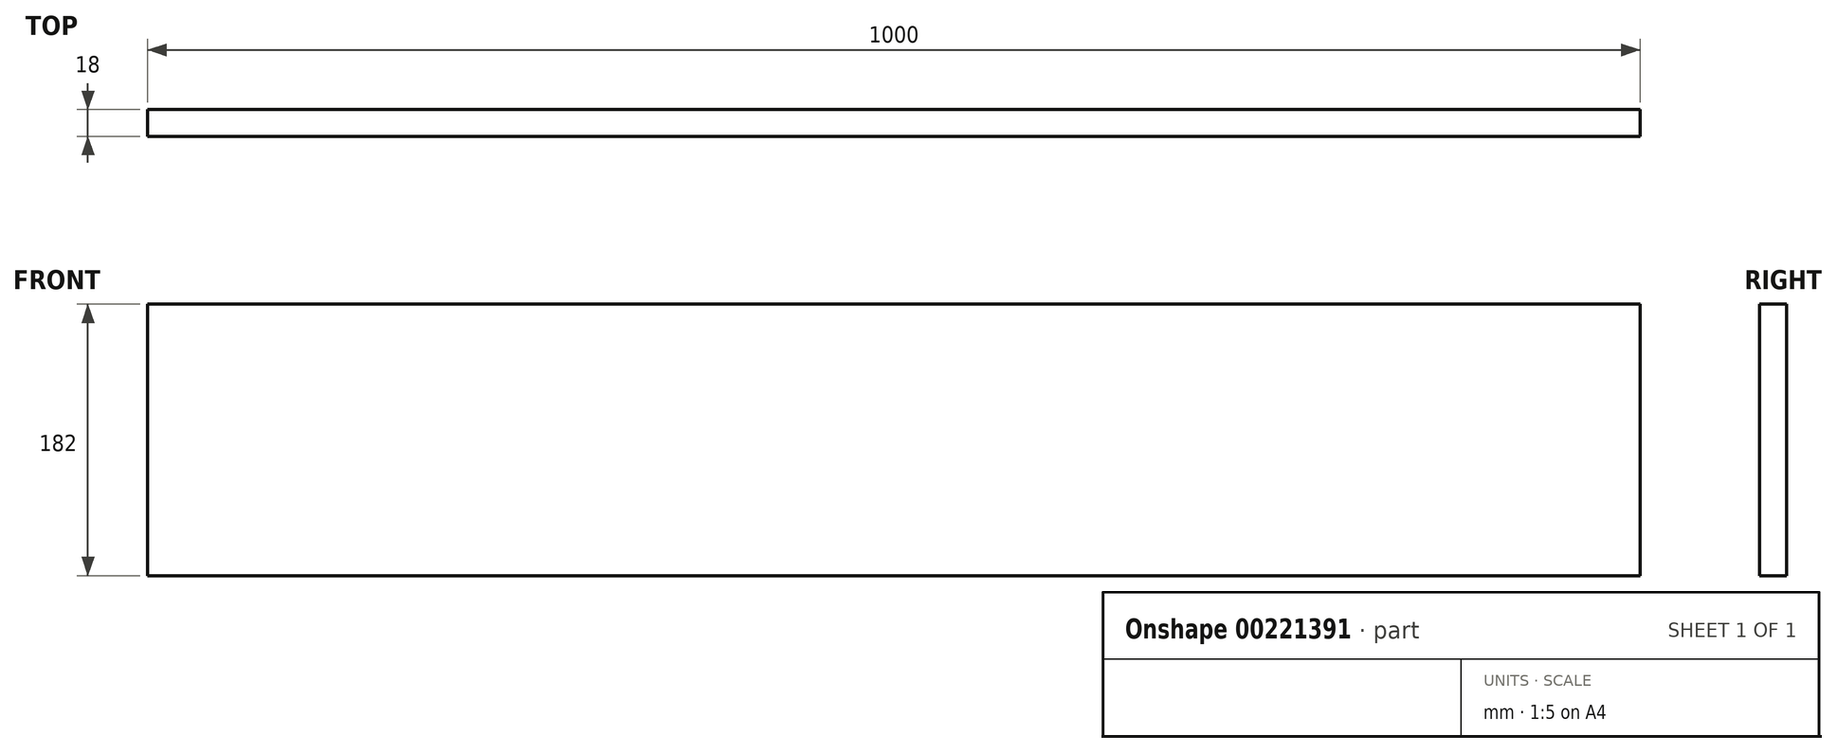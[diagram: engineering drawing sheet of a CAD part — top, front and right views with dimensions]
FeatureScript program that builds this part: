
annotation { "Feature Type Name" : "Feature", "Feature Type Description" : "" }
export const myFeature = defineFeature(function(context is Context, id is Id, definition is map)
    precondition{}
    {
        {
            var Q0;
            Q0=qCreatedBy(makeId("Front.planeOp"),FACE);
            var sketch = newSketch(context, id + "F0", { "sketchPlane" : qUnion([Q0])});
            skLineSegment(sketch, "E0.bottom", {"start": v(500, -91) * mm, "end": v(-500, -91) * mm});
            skLineSegment(sketch, "E0.top", {"start": v(500, 91) * mm, "end": v(-500, 91) * mm});
            skLineSegment(sketch, "E0.left", {"start": v(500, -91) * mm, "end": v(500, 91) * mm});
            skLineSegment(sketch, "E0.right", {"start": v(-500, -91) * mm, "end": v(-500, 91) * mm});
            skPoint(sketch, "E0.middle", {"position": v(0, 0) * mm});
            skSolve(sketch);
        }
        {
            var Q0;
            Q0=qSketchRegion(id+"F0",true);
            extrude(context, id + "F1", {"entities" : qUnion([Q0]), "depth" : 18 * mm});
        }
    });
